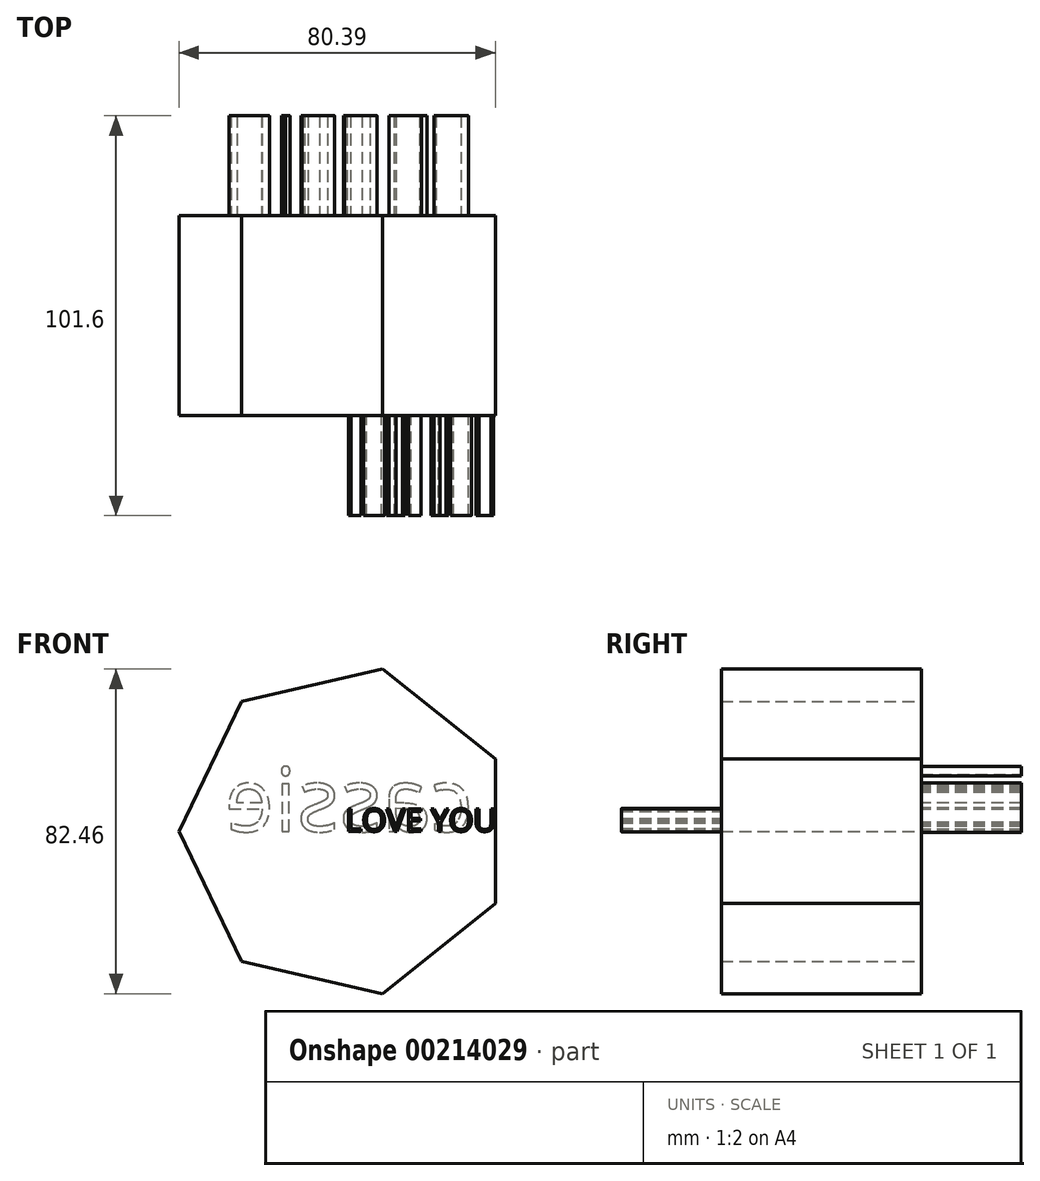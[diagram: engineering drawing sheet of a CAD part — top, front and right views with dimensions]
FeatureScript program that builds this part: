
annotation { "Feature Type Name" : "Feature", "Feature Type Description" : "" }
export const myFeature = defineFeature(function(context is Context, id is Id, definition is map)
    precondition{}
    {
        {
            var Q0;
            Q0=qCreatedBy(makeId("Front.planeOp"),FACE);
            var sketch = newSketch(context, id + "F0", { "sketchPlane" : qUnion([Q0])});
            skCircle(sketch, "E0.cCircle", {"center": v(0, 0) * mm, "radius": 38.1 * mm, "construction": true});
            skLineSegment(sketch, "E0.0", {"start": v(38.1, 18.35) * mm, "end": v(38.1, -18.35) * mm});
            skLineSegment(sketch, "E0.1", {"start": v(38.1, -18.35) * mm, "end": v(9.4, -41.23) * mm});
            skLineSegment(sketch, "E0.2", {"start": v(9.4, -41.23) * mm, "end": v(-26.37, -33.06) * mm});
            skLineSegment(sketch, "E0.3", {"start": v(-26.37, -33.06) * mm, "end": v(-42.29, 0) * mm});
            skLineSegment(sketch, "E0.4", {"start": v(-42.29, 0) * mm, "end": v(-26.37, 33.06) * mm});
            skLineSegment(sketch, "E0.5", {"start": v(-26.37, 33.06) * mm, "end": v(9.4, 41.23) * mm});
            skLineSegment(sketch, "E0.6", {"start": v(9.4, 41.23) * mm, "end": v(38.1, 18.35) * mm});
            skPoint(sketch, "E0.0.midPoint", {"position": v(38.1, 0) * mm});
            skSolve(sketch);
        }
        {
            var Q0;
            Q0 = qSketchRegion(id + "F0", true);
            extrude(context, id + "F1", {"entities" : qUnion([Q0]), "depth" : 25.4 * mm});
        }
        {
            var Q0;
            Q0=makeQuery(id+"F1.opExtrude","CAP_FACE",FACE,{"disambiguationData":[OSD([sQuery(id+"F0.wireOp",EDGE,"E0.0"),sQuery(id+"F0.wireOp",EDGE,"E0.1"),sQuery(id+"F0.wireOp",EDGE,"E0.2"),sQuery(id+"F0.wireOp",EDGE,"E0.3"),sQuery(id+"F0.wireOp",EDGE,"E0.4"),sQuery(id+"F0.wireOp",EDGE,"E0.5"),sQuery(id+"F0.wireOp",EDGE,"E0.6")])],"isStart":false});
            var sketch = newSketch(context, id + "F2", { "sketchPlane" : qUnion([Q0])});
            skText(sketch, "E1", { "text": "LOVE YOU", "fontName": "OpenSans-Regular.ttf"});
            const initialGuessF2  = {"E1": [0, 0, 1, 0, 0.00578]};
            skSetInitialGuess(sketch, initialGuessF2);
            skSolve(sketch);
        }
        {
            var Q0;
            Q0 = qSketchRegion(id + "F2", true);
            extrude(context, id + "F3", {"entities" : qUnion([Q0]), "operationType" : NewBodyOperationType.ADD, "depth" : 25.4 * mm});
        }
        {
            var Q0;
            Q0=makeQuery(id+"F1.opExtrude","CAP_FACE",FACE,{"disambiguationData":[OSD([sQuery(id+"F0.wireOp",EDGE,"E0.0"),sQuery(id+"F0.wireOp",EDGE,"E0.1"),sQuery(id+"F0.wireOp",EDGE,"E0.2"),sQuery(id+"F0.wireOp",EDGE,"E0.3"),sQuery(id+"F0.wireOp",EDGE,"E0.4"),sQuery(id+"F0.wireOp",EDGE,"E0.5"),sQuery(id+"F0.wireOp",EDGE,"E0.6")])],"isStart":true});
            var sketch = newSketch(context, id + "F4", { "sketchPlane" : qUnion([Q0])});
            skSolve(sketch);
        }
        {
            var Q0;
            Q0 = qSketchRegion(id + "F4", true);
            var Q1;
            Q1=makeQuery(id+"F4.imprint","IMPRINT",FACE,{"disambiguationData":[TD([[makeQuery(id+"F4.imprint","IMPRINT",EDGE,{"derivedFrom":makeQuery(id+"F1.opExtrude","CAP_EDGE",EDGE,{"disambiguationData":[OSD([sQuery(id+"F0.wireOp",EDGE,"E0.0")])],"isStart":true})}),1.0]])]});
            extrude(context, id + "F5", {"entities" : qUnion([Q0, Q1]), "operationType" : NewBodyOperationType.ADD, "depth" : 25.4 * mm});
        }
        {
            var Q0;
            Q0=makeQuery(id+"F5.opExtrude","CAP_FACE",FACE,{"disambiguationData":[OSD([sQuery(id+"F0.wireOp",EDGE,"E0.0"),sQuery(id+"F0.wireOp",EDGE,"E0.1"),sQuery(id+"F0.wireOp",EDGE,"E0.2"),sQuery(id+"F0.wireOp",EDGE,"E0.3"),sQuery(id+"F0.wireOp",EDGE,"E0.4"),sQuery(id+"F0.wireOp",EDGE,"E0.5"),sQuery(id+"F0.wireOp",EDGE,"E0.6")])],"isStart":false});
            var sketch = newSketch(context, id + "F6", { "sketchPlane" : qUnion([Q0])});
            skText(sketch, "E2", { "text": "cassie", "fontName": "OpenSans-Regular.ttf"});
            const initialGuessF6  = {"E2": [-0.0325, 0, 1, 0, 0.01625]};
            skSetInitialGuess(sketch, initialGuessF6);
            skSolve(sketch);
        }
        {
            var Q0;
            Q0 = qSketchRegion(id + "F6", true);
            extrude(context, id + "F7", {"entities" : qUnion([Q0]), "operationType" : NewBodyOperationType.ADD, "depth" : 25.4 * mm});
        }
    });
